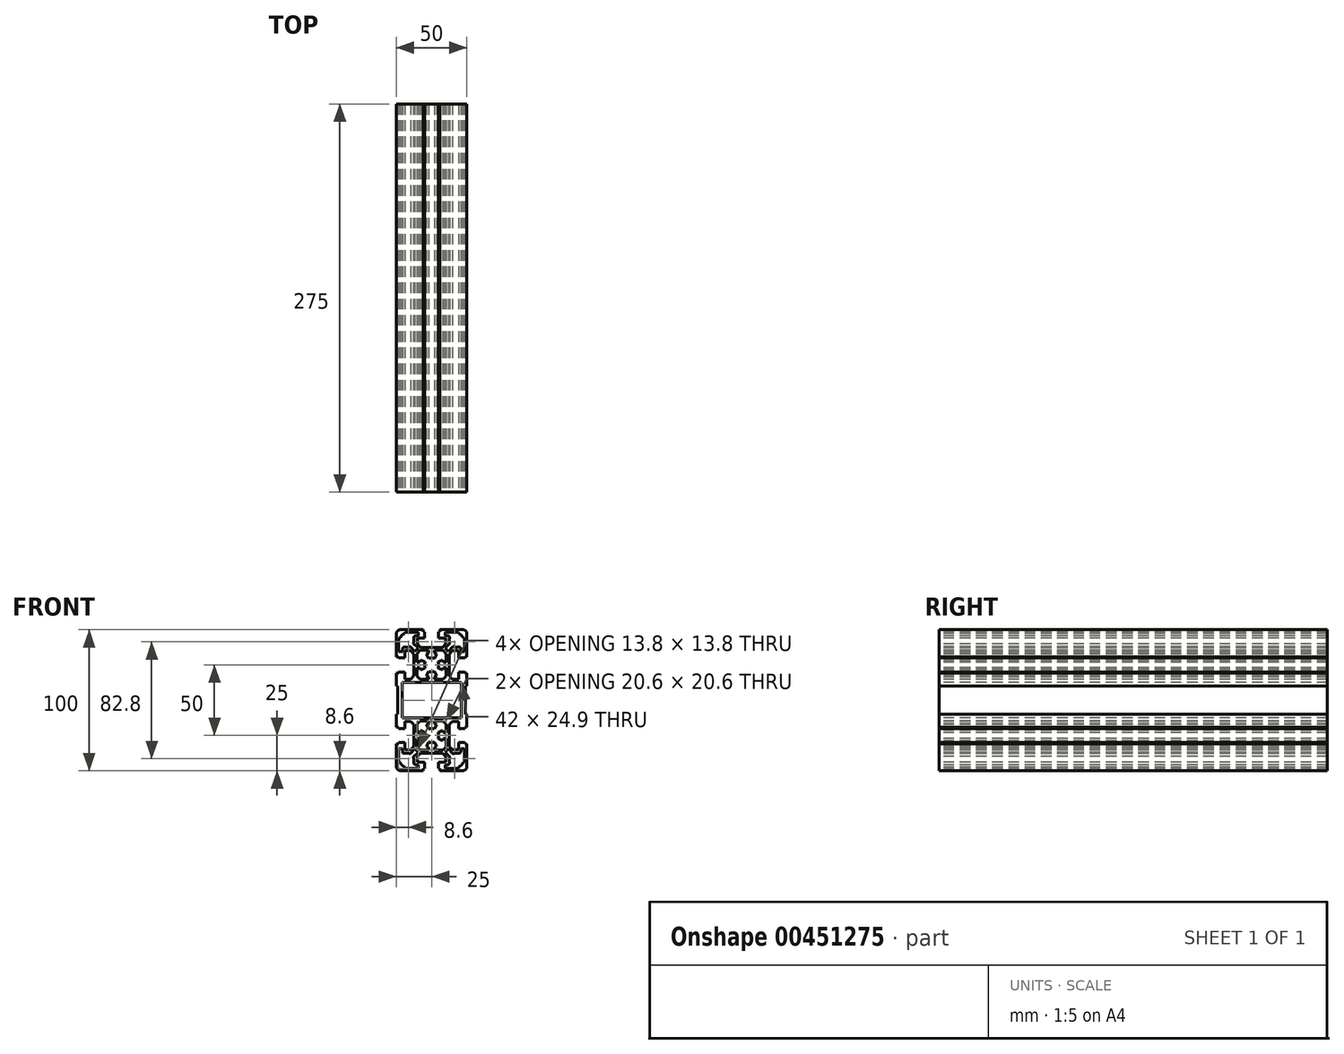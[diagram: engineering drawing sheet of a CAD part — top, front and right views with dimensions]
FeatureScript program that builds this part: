
annotation { "Feature Type Name" : "Feature", "Feature Type Description" : "" }
export const myFeature = defineFeature(function(context is Context, id is Id, definition is map)
    precondition{}
    {
        {
            var Q0;
            Q0=qCreatedBy(makeId("Front.planeOp"),FACE);
            var sketch = newSketch(context, id + "F0", { "sketchPlane" : qUnion([Q0])});
            skLineSegment(sketch, "E0", {"start": v(0, 0) * mm, "end": v(0, 25) * mm, "construction": true});
            skLineSegment(sketch, "E1", {"start": v(0, 0) * mm, "end": v(0, -25) * mm, "construction": true});
            skCircle(sketch, "E2", {"center": v(0, 25) * mm, "radius": 10 * mm});
            skCircle(sketch, "E3", {"center": v(0, -25) * mm, "radius": 10 * mm});
            skLineSegment(sketch, "E4.bottom", {"start": v(25, 50) * mm, "end": v(-25, 50) * mm});
            skLineSegment(sketch, "E4.top", {"start": v(25, -50) * mm, "end": v(-25, -50) * mm});
            skLineSegment(sketch, "E4.left", {"start": v(25, 50) * mm, "end": v(25, -50) * mm});
            skLineSegment(sketch, "E4.right", {"start": v(-25, 50) * mm, "end": v(-25, -50) * mm});
            skPoint(sketch, "E4.middle", {"position": v(0, 0) * mm});
            skSolve(sketch);
        }
        {
            var Q0;
            Q0=makeQuery(id+"F0.imprint","IMPRINT",FACE,{"disambiguationData":[TD([[makeQuery(id+"F0.imprint","IMPRINT",EDGE,{"derivedFrom":sQuery(id+"F0.wireOp",EDGE,"E2")}),-1.0]])]});
            cPlane(context, id + "F1", {"entities" : qUnion([Q0]), "cplaneType" : CPlaneType.OFFSET, "offset" : 25 * mm, "width" : 150 * mm, "height" : 150 * mm});
        }
        {
            var Q0;
            Q0=qCreatedBy(makeId("Front.planeOp"),FACE);
            var sketch = newSketch(context, id + "F2", { "sketchPlane" : qUnion([Q0])});
            skArc(sketch, "E5", {"start": v(-18.8, 37.67) * mm, "mid": v(-20.11, 37.42) * mm, "end": v(-20.7, 36.23) * mm});
            skArc(sketch, "E6", {"start": v(20.7, 36.23) * mm, "mid": v(20.11, 37.42) * mm, "end": v(18.8, 37.67) * mm});
            skArc(sketch, "E7", {"start": v(12.9, -40.52) * mm, "mid": v(12.51, -42.15) * mm, "end": v(12.67, -43.8) * mm});
            skArc(sketch, "E8", {"start": v(22, -50) * mm, "mid": v(24.12, -49.12) * mm, "end": v(25, -47) * mm});
            skArc(sketch, "E9", {"start": v(19, -47.27) * mm, "mid": v(21.04, -46.04) * mm, "end": v(22.27, -44) * mm});
            skArc(sketch, "E10", {"start": v(11.23, -45.7) * mm, "mid": v(12.42, -45.11) * mm, "end": v(12.67, -43.8) * mm});
            skArc(sketch, "E11", {"start": v(18.8, -37.67) * mm, "mid": v(20.11, -37.42) * mm, "end": v(20.7, -36.23) * mm});
            skArc(sketch, "E12", {"start": v(18.8, -37.67) * mm, "mid": v(17.14, -37.51) * mm, "end": v(15.52, -37.9) * mm});
            skArc(sketch, "E13", {"start": v(15.2, -37.85) * mm, "mid": v(15.35, -37.93) * mm, "end": v(15.52, -37.9) * mm});
            skArc(sketch, "E14", {"start": v(12.9, -40.52) * mm, "mid": v(12.93, -40.35) * mm, "end": v(12.84, -40.2) * mm});
            skArc(sketch, "E15", {"start": v(-4.53, -22.89) * mm, "mid": v(-5, -25) * mm, "end": v(-4.53, -27.11) * mm});
            skArc(sketch, "E16", {"start": v(4.53, -27.11) * mm, "mid": v(5, -25) * mm, "end": v(4.53, -22.89) * mm});
            skArc(sketch, "E17", {"start": v(-2.11, -29.53) * mm, "mid": v(0, -30) * mm, "end": v(2.11, -29.53) * mm});
            skArc(sketch, "E18", {"start": v(2.11, -20.47) * mm, "mid": v(0, -20) * mm, "end": v(-2.11, -20.47) * mm});
            skArc(sketch, "E19", {"start": v(-4.53, 27.11) * mm, "mid": v(-5, 25) * mm, "end": v(-4.53, 22.89) * mm});
            skArc(sketch, "E20", {"start": v(4.53, 22.89) * mm, "mid": v(5, 25) * mm, "end": v(4.53, 27.11) * mm});
            skArc(sketch, "E21", {"start": v(-2.11, 20.47) * mm, "mid": v(0, 20) * mm, "end": v(2.11, 20.47) * mm});
            skArc(sketch, "E22", {"start": v(15.52, 37.9) * mm, "mid": v(15.35, 37.93) * mm, "end": v(15.2, 37.84) * mm});
            skArc(sketch, "E23", {"start": v(15.52, 37.9) * mm, "mid": v(17.14, 37.51) * mm, "end": v(18.8, 37.67) * mm});
            skArc(sketch, "E24", {"start": v(2.11, 29.53) * mm, "mid": v(0, 30) * mm, "end": v(-2.11, 29.53) * mm});
            skArc(sketch, "E25", {"start": v(-12.67, -43.8) * mm, "mid": v(-12.51, -42.15) * mm, "end": v(-12.9, -40.52) * mm});
            skArc(sketch, "E26", {"start": v(-25, -47) * mm, "mid": v(-24.12, -49.12) * mm, "end": v(-22, -50) * mm});
            skArc(sketch, "E27", {"start": v(-12.67, -43.8) * mm, "mid": v(-12.42, -45.11) * mm, "end": v(-11.23, -45.7) * mm});
            skArc(sketch, "E28", {"start": v(-22.27, -44) * mm, "mid": v(-21.04, -46.04) * mm, "end": v(-19, -47.27) * mm});
            skArc(sketch, "E29", {"start": v(-20.7, -36.23) * mm, "mid": v(-20.11, -37.42) * mm, "end": v(-18.8, -37.67) * mm});
            skArc(sketch, "E30", {"start": v(-15.52, -37.9) * mm, "mid": v(-17.14, -37.51) * mm, "end": v(-18.8, -37.67) * mm});
            skArc(sketch, "E31", {"start": v(-12.84, -40.2) * mm, "mid": v(-12.93, -40.35) * mm, "end": v(-12.9, -40.52) * mm});
            skArc(sketch, "E32", {"start": v(-15.52, -37.9) * mm, "mid": v(-15.35, -37.93) * mm, "end": v(-15.2, -37.85) * mm});
            skArc(sketch, "E33", {"start": v(-18.8, 37.67) * mm, "mid": v(-17.14, 37.51) * mm, "end": v(-15.52, 37.9) * mm});
            skArc(sketch, "E34", {"start": v(-15.2, 37.84) * mm, "mid": v(-15.35, 37.93) * mm, "end": v(-15.52, 37.9) * mm});
            skArc(sketch, "E35", {"start": v(25, 47) * mm, "mid": v(24.12, 49.12) * mm, "end": v(22, 50) * mm});
            skArc(sketch, "E36", {"start": v(22.27, 44) * mm, "mid": v(21.04, 46.04) * mm, "end": v(19, 47.27) * mm});
            skArc(sketch, "E37", {"start": v(12.67, 43.8) * mm, "mid": v(12.42, 45.11) * mm, "end": v(11.23, 45.7) * mm});
            skArc(sketch, "E38", {"start": v(12.67, 43.8) * mm, "mid": v(12.51, 42.14) * mm, "end": v(12.9, 40.52) * mm});
            skArc(sketch, "E39", {"start": v(12.84, 40.2) * mm, "mid": v(12.93, 40.35) * mm, "end": v(12.9, 40.52) * mm});
            skArc(sketch, "E40", {"start": v(-22, 50) * mm, "mid": v(-24.12, 49.12) * mm, "end": v(-25, 47) * mm});
            skArc(sketch, "E41", {"start": v(-11.23, 45.7) * mm, "mid": v(-12.42, 45.11) * mm, "end": v(-12.67, 43.8) * mm});
            skArc(sketch, "E42", {"start": v(-12.9, 40.52) * mm, "mid": v(-12.93, 40.35) * mm, "end": v(-12.84, 40.2) * mm});
            skArc(sketch, "E43", {"start": v(-12.9, 40.52) * mm, "mid": v(-12.51, 42.14) * mm, "end": v(-12.67, 43.8) * mm});
            skArc(sketch, "E44", {"start": v(-19, 47.27) * mm, "mid": v(-21.04, 46.04) * mm, "end": v(-22.27, 44) * mm});
            skLineSegment(sketch, "E45", {"start": v(-9.54, 36.88) * mm, "end": v(-12.84, 40.2) * mm});
            skLineSegment(sketch, "E46", {"start": v(-25, 47) * mm, "end": v(-25, 30.8) * mm});
            skLineSegment(sketch, "E47", {"start": v(-23.3, 44) * mm, "end": v(-23.3, 34.5) * mm});
            skLineSegment(sketch, "E48", {"start": v(10.05, 39.8) * mm, "end": v(7.75, 37.5) * mm});
            skLineSegment(sketch, "E49", {"start": v(12.84, 40.2) * mm, "end": v(9.54, 36.88) * mm});
            skLineSegment(sketch, "E50", {"start": v(25, 30.8) * mm, "end": v(25, 47) * mm});
            skLineSegment(sketch, "E51", {"start": v(23.3, 34.5) * mm, "end": v(23.3, 44) * mm});
            skLineSegment(sketch, "E52", {"start": v(-7.75, 37.5) * mm, "end": v(-10.05, 39.8) * mm});
            skLineSegment(sketch, "E53", {"start": v(-2, 35.3) * mm, "end": v(-8.01, 35.3) * mm});
            skLineSegment(sketch, "E54", {"start": v(7.75, 37.5) * mm, "end": v(-7.75, 37.5) * mm});
            skLineSegment(sketch, "E55", {"start": v(-4.53, 22.89) * mm, "end": v(-7.7, 21.4) * mm});
            skLineSegment(sketch, "E56", {"start": v(-8.01, 14.7) * mm, "end": v(-2, 14.7) * mm});
            skLineSegment(sketch, "E57", {"start": v(-7.7, 28.6) * mm, "end": v(-4.53, 27.11) * mm});
            skLineSegment(sketch, "E58", {"start": v(-8.01, -35.3) * mm, "end": v(-2, -35.3) * mm});
            skLineSegment(sketch, "E59", {"start": v(-2, -14.7) * mm, "end": v(-8.01, -14.7) * mm});
            skLineSegment(sketch, "E60", {"start": v(-7.7, -21.4) * mm, "end": v(-4.53, -22.89) * mm});
            skLineSegment(sketch, "E61", {"start": v(-4.53, -27.11) * mm, "end": v(-7.7, -28.6) * mm});
            skLineSegment(sketch, "E62", {"start": v(-7.75, -37.5) * mm, "end": v(7.75, -37.5) * mm});
            skLineSegment(sketch, "E63", {"start": v(-5, -44) * mm, "end": v(-10.05, -44) * mm});
            skLineSegment(sketch, "E64", {"start": v(-22, -50) * mm, "end": v(-5.8, -50) * mm});
            skLineSegment(sketch, "E65", {"start": v(21, 12.45) * mm, "end": v(-21, 12.45) * mm});
            skLineSegment(sketch, "E66", {"start": v(-21, -12.45) * mm, "end": v(21, -12.45) * mm});
            skLineSegment(sketch, "E67", {"start": v(24, -10) * mm, "end": v(24, 10) * mm});
            skLineSegment(sketch, "E68", {"start": v(21, -12.45) * mm, "end": v(21, 12.45) * mm});
            skLineSegment(sketch, "E69", {"start": v(-3.6, -32.7) * mm, "end": v(-2.11, -29.53) * mm});
            skLineSegment(sketch, "E70", {"start": v(2.11, -29.53) * mm, "end": v(3.6, -32.7) * mm});
            skLineSegment(sketch, "E71", {"start": v(10.3, -33.01) * mm, "end": v(10.3, -27) * mm});
            skLineSegment(sketch, "E72", {"start": v(12.5, -32.75) * mm, "end": v(12.5, -17.25) * mm});
            skLineSegment(sketch, "E73", {"start": v(19, -30) * mm, "end": v(19, -35.05) * mm});
            skLineSegment(sketch, "E74", {"start": v(25, -47) * mm, "end": v(25, -30.8) * mm});
            skLineSegment(sketch, "E75", {"start": v(10.05, -39.8) * mm, "end": v(10.05, -44) * mm});
            skLineSegment(sketch, "E76", {"start": v(23.3, -44) * mm, "end": v(23.3, -34.5) * mm});
            skLineSegment(sketch, "E77", {"start": v(5.8, -50) * mm, "end": v(22, -50) * mm});
            skLineSegment(sketch, "E78", {"start": v(9.5, -48.3) * mm, "end": v(19, -48.3) * mm});
            skLineSegment(sketch, "E79", {"start": v(22.27, -44) * mm, "end": v(23.3, -44) * mm});
            skLineSegment(sketch, "E80", {"start": v(19, -48.3) * mm, "end": v(19, -47.27) * mm});
            skLineSegment(sketch, "E81", {"start": v(-5.8, -50) * mm, "end": v(-5.8, -48.5) * mm});
            skLineSegment(sketch, "E82", {"start": v(5.8, -48.5) * mm, "end": v(5.8, -50) * mm});
            skLineSegment(sketch, "E83", {"start": v(10.05, -44) * mm, "end": v(5, -44) * mm});
            skLineSegment(sketch, "E84", {"start": v(11.23, -45.7) * mm, "end": v(9.5, -45.7) * mm});
            skLineSegment(sketch, "E85", {"start": v(5, -48.5) * mm, "end": v(5.8, -48.5) * mm});
            skLineSegment(sketch, "E86", {"start": v(5, -44) * mm, "end": v(5, -48.5) * mm});
            skLineSegment(sketch, "E87", {"start": v(9.5, -45.7) * mm, "end": v(9.5, -48.3) * mm});
            skLineSegment(sketch, "E88", {"start": v(-5.8, -48.5) * mm, "end": v(-5, -48.5) * mm});
            skLineSegment(sketch, "E89", {"start": v(-5, -48.5) * mm, "end": v(-5, -44) * mm});
            skLineSegment(sketch, "E90", {"start": v(14.8, -35.05) * mm, "end": v(12.5, -32.75) * mm});
            skLineSegment(sketch, "E91", {"start": v(15.2, -37.85) * mm, "end": v(11.88, -34.54) * mm});
            skLineSegment(sketch, "E92", {"start": v(19, -35.05) * mm, "end": v(14.8, -35.05) * mm});
            skLineSegment(sketch, "E93", {"start": v(20.7, -34.5) * mm, "end": v(20.7, -36.23) * mm});
            skLineSegment(sketch, "E94", {"start": v(23.3, -34.5) * mm, "end": v(20.7, -34.5) * mm});
            skLineSegment(sketch, "E95", {"start": v(9.54, -36.89) * mm, "end": v(12.84, -40.2) * mm});
            skLineSegment(sketch, "E96", {"start": v(7.75, -37.5) * mm, "end": v(10.05, -39.8) * mm});
            skLineSegment(sketch, "E97", {"start": v(3.6, -32.7) * mm, "end": v(2, -33.45) * mm});
            skLineSegment(sketch, "E98", {"start": v(2, -35.3) * mm, "end": v(8.01, -35.3) * mm});
            skLineSegment(sketch, "E99", {"start": v(11.88, -34.54) * mm, "end": v(9.54, -36.89) * mm});
            skLineSegment(sketch, "E100", {"start": v(8.01, -35.3) * mm, "end": v(10.3, -33.01) * mm});
            skLineSegment(sketch, "E101", {"start": v(-2, -35.3) * mm, "end": v(-2, -33.45) * mm});
            skLineSegment(sketch, "E102", {"start": v(-2, -33.45) * mm, "end": v(-3.6, -32.7) * mm});
            skLineSegment(sketch, "E103", {"start": v(2, -33.45) * mm, "end": v(2, -35.3) * mm});
            skLineSegment(sketch, "E104", {"start": v(-2.11, -20.47) * mm, "end": v(-3.6, -17.3) * mm});
            skLineSegment(sketch, "E105", {"start": v(10.3, -23) * mm, "end": v(10.3, -16.99) * mm});
            skLineSegment(sketch, "E106", {"start": v(3.6, -17.3) * mm, "end": v(2.11, -20.47) * mm});
            skLineSegment(sketch, "E107", {"start": v(19, -14.95) * mm, "end": v(19, -20) * mm});
            skLineSegment(sketch, "E108", {"start": v(23.5, -20) * mm, "end": v(23.5, -19.2) * mm});
            skLineSegment(sketch, "E109", {"start": v(25, -30.8) * mm, "end": v(23.5, -30.8) * mm});
            skLineSegment(sketch, "E110", {"start": v(23.5, -30.8) * mm, "end": v(23.5, -30) * mm});
            skLineSegment(sketch, "E111", {"start": v(23.5, -30) * mm, "end": v(19, -30) * mm});
            skLineSegment(sketch, "E112", {"start": v(19, -20) * mm, "end": v(23.5, -20) * mm});
            skLineSegment(sketch, "E113", {"start": v(10.3, -27) * mm, "end": v(8.45, -27) * mm});
            skLineSegment(sketch, "E114", {"start": v(8.45, -27) * mm, "end": v(7.7, -28.6) * mm});
            skLineSegment(sketch, "E115", {"start": v(7.7, -28.6) * mm, "end": v(4.53, -27.11) * mm});
            skLineSegment(sketch, "E116", {"start": v(4.53, -22.89) * mm, "end": v(7.7, -21.4) * mm});
            skLineSegment(sketch, "E117", {"start": v(7.7, -21.4) * mm, "end": v(8.45, -23) * mm});
            skLineSegment(sketch, "E118", {"start": v(8.45, -23) * mm, "end": v(10.3, -23) * mm});
            skLineSegment(sketch, "E119", {"start": v(12.5, -17.25) * mm, "end": v(14.8, -14.95) * mm});
            skLineSegment(sketch, "E120", {"start": v(25, -19.2) * mm, "end": v(25, -10) * mm});
            skLineSegment(sketch, "E121", {"start": v(23.5, -19.2) * mm, "end": v(25, -19.2) * mm});
            skLineSegment(sketch, "E122", {"start": v(14.8, -14.95) * mm, "end": v(19, -14.95) * mm});
            skLineSegment(sketch, "E123", {"start": v(25, -10) * mm, "end": v(24, -10) * mm});
            skLineSegment(sketch, "E124", {"start": v(8.01, -14.7) * mm, "end": v(2, -14.7) * mm});
            skLineSegment(sketch, "E125", {"start": v(2, -16.55) * mm, "end": v(3.6, -17.3) * mm});
            skLineSegment(sketch, "E126", {"start": v(10.3, -16.99) * mm, "end": v(8.01, -14.7) * mm});
            skLineSegment(sketch, "E127", {"start": v(-3.6, -17.3) * mm, "end": v(-2, -16.55) * mm});
            skLineSegment(sketch, "E128", {"start": v(-2, -16.55) * mm, "end": v(-2, -14.7) * mm});
            skLineSegment(sketch, "E129", {"start": v(2, -14.7) * mm, "end": v(2, -16.55) * mm});
            skLineSegment(sketch, "E130", {"start": v(-2, 14.7) * mm, "end": v(-2, 16.55) * mm});
            skLineSegment(sketch, "E131", {"start": v(2, 16.55) * mm, "end": v(2, 14.7) * mm});
            skLineSegment(sketch, "E132", {"start": v(8.01, 14.7) * mm, "end": v(10.3, 16.99) * mm});
            skLineSegment(sketch, "E133", {"start": v(25, 10) * mm, "end": v(25, 19.2) * mm});
            skLineSegment(sketch, "E134", {"start": v(24, 10) * mm, "end": v(25, 10) * mm});
            skLineSegment(sketch, "E135", {"start": v(2, 14.7) * mm, "end": v(8.01, 14.7) * mm});
            skLineSegment(sketch, "E136", {"start": v(12.5, 17.25) * mm, "end": v(12.5, 32.75) * mm});
            skLineSegment(sketch, "E137", {"start": v(14.8, 14.95) * mm, "end": v(12.5, 17.25) * mm});
            skLineSegment(sketch, "E138", {"start": v(25, 19.2) * mm, "end": v(23.5, 19.2) * mm});
            skLineSegment(sketch, "E139", {"start": v(19, 14.95) * mm, "end": v(14.8, 14.95) * mm});
            skLineSegment(sketch, "E140", {"start": v(19, 20) * mm, "end": v(19, 14.95) * mm});
            skLineSegment(sketch, "E141", {"start": v(23.5, 19.2) * mm, "end": v(23.5, 20) * mm});
            skLineSegment(sketch, "E142", {"start": v(23.5, 20) * mm, "end": v(19, 20) * mm});
            skLineSegment(sketch, "E143", {"start": v(10.3, 16.99) * mm, "end": v(10.3, 23) * mm});
            skLineSegment(sketch, "E144", {"start": v(2.11, 20.47) * mm, "end": v(3.6, 17.3) * mm});
            skLineSegment(sketch, "E145", {"start": v(3.6, 17.3) * mm, "end": v(2, 16.55) * mm});
            skLineSegment(sketch, "E146", {"start": v(-2, 16.55) * mm, "end": v(-3.6, 17.3) * mm});
            skLineSegment(sketch, "E147", {"start": v(-3.6, 17.3) * mm, "end": v(-2.11, 20.47) * mm});
            skLineSegment(sketch, "E148", {"start": v(10.3, 23) * mm, "end": v(8.45, 23) * mm});
            skLineSegment(sketch, "E149", {"start": v(8.45, 23) * mm, "end": v(7.7, 21.4) * mm});
            skLineSegment(sketch, "E150", {"start": v(7.7, 21.4) * mm, "end": v(4.53, 22.89) * mm});
            skLineSegment(sketch, "E151", {"start": v(12.5, 32.75) * mm, "end": v(14.8, 35.05) * mm});
            skLineSegment(sketch, "E152", {"start": v(11.88, 34.54) * mm, "end": v(15.2, 37.84) * mm});
            skLineSegment(sketch, "E153", {"start": v(19, 35.05) * mm, "end": v(19, 30) * mm});
            skLineSegment(sketch, "E154", {"start": v(23.5, 30.8) * mm, "end": v(25, 30.8) * mm});
            skLineSegment(sketch, "E155", {"start": v(23.5, 30) * mm, "end": v(23.5, 30.8) * mm});
            skLineSegment(sketch, "E156", {"start": v(19, 30) * mm, "end": v(23.5, 30) * mm});
            skLineSegment(sketch, "E157", {"start": v(14.8, 35.05) * mm, "end": v(19, 35.05) * mm});
            skLineSegment(sketch, "E158", {"start": v(20.7, 34.5) * mm, "end": v(23.3, 34.5) * mm});
            skLineSegment(sketch, "E159", {"start": v(20.7, 36.23) * mm, "end": v(20.7, 34.5) * mm});
            skLineSegment(sketch, "E160", {"start": v(-2.11, 29.53) * mm, "end": v(-3.6, 32.7) * mm});
            skLineSegment(sketch, "E161", {"start": v(10.3, 27) * mm, "end": v(10.3, 33.01) * mm});
            skLineSegment(sketch, "E162", {"start": v(3.6, 32.7) * mm, "end": v(2.11, 29.53) * mm});
            skLineSegment(sketch, "E163", {"start": v(4.53, 27.11) * mm, "end": v(7.7, 28.6) * mm});
            skLineSegment(sketch, "E164", {"start": v(7.7, 28.6) * mm, "end": v(8.45, 27) * mm});
            skLineSegment(sketch, "E165", {"start": v(8.45, 27) * mm, "end": v(10.3, 27) * mm});
            skLineSegment(sketch, "E166", {"start": v(8.01, 35.3) * mm, "end": v(2, 35.3) * mm});
            skLineSegment(sketch, "E167", {"start": v(2, 33.45) * mm, "end": v(3.6, 32.7) * mm});
            skLineSegment(sketch, "E168", {"start": v(10.3, 33.01) * mm, "end": v(8.01, 35.3) * mm});
            skLineSegment(sketch, "E169", {"start": v(9.54, 36.88) * mm, "end": v(11.88, 34.54) * mm});
            skLineSegment(sketch, "E170", {"start": v(-3.6, 32.7) * mm, "end": v(-2, 33.45) * mm});
            skLineSegment(sketch, "E171", {"start": v(2, 35.3) * mm, "end": v(2, 33.45) * mm});
            skLineSegment(sketch, "E172", {"start": v(-2, 33.45) * mm, "end": v(-2, 35.3) * mm});
            skLineSegment(sketch, "E173", {"start": v(-24, 10) * mm, "end": v(-24, -10) * mm});
            skLineSegment(sketch, "E174", {"start": v(-21, 12.45) * mm, "end": v(-21, -12.45) * mm});
            skLineSegment(sketch, "E175", {"start": v(-19, -35.05) * mm, "end": v(-19, -30) * mm});
            skLineSegment(sketch, "E176", {"start": v(-12.5, -17.25) * mm, "end": v(-12.5, -32.75) * mm});
            skLineSegment(sketch, "E177", {"start": v(-10.3, -27) * mm, "end": v(-10.3, -33.01) * mm});
            skLineSegment(sketch, "E178", {"start": v(-25, -30.8) * mm, "end": v(-25, -47) * mm});
            skLineSegment(sketch, "E179", {"start": v(-23.3, -34.5) * mm, "end": v(-23.3, -44) * mm});
            skLineSegment(sketch, "E180", {"start": v(-10.05, -44) * mm, "end": v(-10.05, -39.8) * mm});
            skLineSegment(sketch, "E181", {"start": v(-19, -48.3) * mm, "end": v(-9.5, -48.3) * mm});
            skLineSegment(sketch, "E182", {"start": v(-9.5, -45.7) * mm, "end": v(-11.23, -45.7) * mm});
            skLineSegment(sketch, "E183", {"start": v(-9.5, -48.3) * mm, "end": v(-9.5, -45.7) * mm});
            skLineSegment(sketch, "E184", {"start": v(-23.3, -44) * mm, "end": v(-22.27, -44) * mm});
            skLineSegment(sketch, "E185", {"start": v(-19, -47.27) * mm, "end": v(-19, -48.3) * mm});
            skLineSegment(sketch, "E186", {"start": v(-12.84, -40.2) * mm, "end": v(-9.54, -36.89) * mm});
            skLineSegment(sketch, "E187", {"start": v(-11.88, -34.54) * mm, "end": v(-15.2, -37.85) * mm});
            skLineSegment(sketch, "E188", {"start": v(-10.05, -39.8) * mm, "end": v(-7.75, -37.5) * mm});
            skLineSegment(sketch, "E189", {"start": v(-14.8, -35.05) * mm, "end": v(-19, -35.05) * mm});
            skLineSegment(sketch, "E190", {"start": v(-12.5, -32.75) * mm, "end": v(-14.8, -35.05) * mm});
            skLineSegment(sketch, "E191", {"start": v(-9.54, -36.89) * mm, "end": v(-11.88, -34.54) * mm});
            skLineSegment(sketch, "E192", {"start": v(-10.3, -33.01) * mm, "end": v(-8.01, -35.3) * mm});
            skLineSegment(sketch, "E193", {"start": v(-20.7, -36.23) * mm, "end": v(-20.7, -34.5) * mm});
            skLineSegment(sketch, "E194", {"start": v(-20.7, -34.5) * mm, "end": v(-23.3, -34.5) * mm});
            skLineSegment(sketch, "E195", {"start": v(-23.5, -19.2) * mm, "end": v(-23.5, -20) * mm});
            skLineSegment(sketch, "E196", {"start": v(-19, -20) * mm, "end": v(-19, -14.95) * mm});
            skLineSegment(sketch, "E197", {"start": v(-10.3, -16.99) * mm, "end": v(-10.3, -23) * mm});
            skLineSegment(sketch, "E198", {"start": v(-7.7, -28.6) * mm, "end": v(-8.45, -27) * mm});
            skLineSegment(sketch, "E199", {"start": v(-8.45, -27) * mm, "end": v(-10.3, -27) * mm});
            skLineSegment(sketch, "E200", {"start": v(-23.5, -30.8) * mm, "end": v(-25, -30.8) * mm});
            skLineSegment(sketch, "E201", {"start": v(-23.5, -30) * mm, "end": v(-23.5, -30.8) * mm});
            skLineSegment(sketch, "E202", {"start": v(-19, -30) * mm, "end": v(-23.5, -30) * mm});
            skLineSegment(sketch, "E203", {"start": v(-8.45, -23) * mm, "end": v(-7.7, -21.4) * mm});
            skLineSegment(sketch, "E204", {"start": v(-10.3, -23) * mm, "end": v(-8.45, -23) * mm});
            skLineSegment(sketch, "E205", {"start": v(-23.5, -20) * mm, "end": v(-19, -20) * mm});
            skLineSegment(sketch, "E206", {"start": v(-25, -10) * mm, "end": v(-25, -19.2) * mm});
            skLineSegment(sketch, "E207", {"start": v(-19, -14.95) * mm, "end": v(-14.8, -14.95) * mm});
            skLineSegment(sketch, "E208", {"start": v(-14.8, -14.95) * mm, "end": v(-12.5, -17.25) * mm});
            skLineSegment(sketch, "E209", {"start": v(-8.01, -14.7) * mm, "end": v(-10.3, -16.99) * mm});
            skLineSegment(sketch, "E210", {"start": v(-25, -19.2) * mm, "end": v(-23.5, -19.2) * mm});
            skLineSegment(sketch, "E211", {"start": v(-24, -10) * mm, "end": v(-25, -10) * mm});
            skLineSegment(sketch, "E212", {"start": v(-25, 19.2) * mm, "end": v(-25, 10) * mm});
            skLineSegment(sketch, "E213", {"start": v(-10.3, 16.99) * mm, "end": v(-8.01, 14.7) * mm});
            skLineSegment(sketch, "E214", {"start": v(-25, 10) * mm, "end": v(-24, 10) * mm});
            skLineSegment(sketch, "E215", {"start": v(-12.5, 32.75) * mm, "end": v(-12.5, 17.25) * mm});
            skLineSegment(sketch, "E216", {"start": v(-10.3, 23) * mm, "end": v(-10.3, 16.99) * mm});
            skLineSegment(sketch, "E217", {"start": v(-14.8, 14.95) * mm, "end": v(-19, 14.95) * mm});
            skLineSegment(sketch, "E218", {"start": v(-12.5, 17.25) * mm, "end": v(-14.8, 14.95) * mm});
            skLineSegment(sketch, "E219", {"start": v(-23.5, 19.2) * mm, "end": v(-25, 19.2) * mm});
            skLineSegment(sketch, "E220", {"start": v(-23.5, 20) * mm, "end": v(-23.5, 19.2) * mm});
            skLineSegment(sketch, "E221", {"start": v(-19, 14.95) * mm, "end": v(-19, 20) * mm});
            skLineSegment(sketch, "E222", {"start": v(-19, 20) * mm, "end": v(-23.5, 20) * mm});
            skLineSegment(sketch, "E223", {"start": v(-7.7, 21.4) * mm, "end": v(-8.45, 23) * mm});
            skLineSegment(sketch, "E224", {"start": v(-8.45, 23) * mm, "end": v(-10.3, 23) * mm});
            skLineSegment(sketch, "E225", {"start": v(-10.3, 33.01) * mm, "end": v(-10.3, 27) * mm});
            skLineSegment(sketch, "E226", {"start": v(-19, 30) * mm, "end": v(-19, 35.05) * mm});
            skLineSegment(sketch, "E227", {"start": v(-8.45, 27) * mm, "end": v(-7.7, 28.6) * mm});
            skLineSegment(sketch, "E228", {"start": v(-10.3, 27) * mm, "end": v(-8.45, 27) * mm});
            skLineSegment(sketch, "E229", {"start": v(-23.5, 30.8) * mm, "end": v(-23.5, 30) * mm});
            skLineSegment(sketch, "E230", {"start": v(-25, 30.8) * mm, "end": v(-23.5, 30.8) * mm});
            skLineSegment(sketch, "E231", {"start": v(-23.5, 30) * mm, "end": v(-19, 30) * mm});
            skLineSegment(sketch, "E232", {"start": v(-19, 35.05) * mm, "end": v(-14.8, 35.05) * mm});
            skLineSegment(sketch, "E233", {"start": v(-14.8, 35.05) * mm, "end": v(-12.5, 32.75) * mm});
            skLineSegment(sketch, "E234", {"start": v(-15.2, 37.84) * mm, "end": v(-11.88, 34.54) * mm});
            skLineSegment(sketch, "E235", {"start": v(-11.88, 34.54) * mm, "end": v(-9.54, 36.88) * mm});
            skLineSegment(sketch, "E236", {"start": v(-8.01, 35.3) * mm, "end": v(-10.3, 33.01) * mm});
            skLineSegment(sketch, "E237", {"start": v(-23.3, 34.5) * mm, "end": v(-20.7, 34.5) * mm});
            skLineSegment(sketch, "E238", {"start": v(-20.7, 34.5) * mm, "end": v(-20.7, 36.23) * mm});
            skLineSegment(sketch, "E239", {"start": v(-5.8, 50) * mm, "end": v(-22, 50) * mm});
            skLineSegment(sketch, "E240", {"start": v(-10.05, 44) * mm, "end": v(-5, 44) * mm});
            skLineSegment(sketch, "E241", {"start": v(-5.8, 48.5) * mm, "end": v(-5.8, 50) * mm});
            skLineSegment(sketch, "E242", {"start": v(5.8, 50) * mm, "end": v(5.8, 48.5) * mm});
            skLineSegment(sketch, "E243", {"start": v(19, 48.3) * mm, "end": v(9.5, 48.3) * mm});
            skLineSegment(sketch, "E244", {"start": v(19, 47.27) * mm, "end": v(19, 48.3) * mm});
            skLineSegment(sketch, "E245", {"start": v(23.3, 44) * mm, "end": v(22.27, 44) * mm});
            skLineSegment(sketch, "E246", {"start": v(10.05, 44) * mm, "end": v(10.05, 39.8) * mm});
            skLineSegment(sketch, "E247", {"start": v(5, 44) * mm, "end": v(10.05, 44) * mm});
            skLineSegment(sketch, "E248", {"start": v(5, 48.5) * mm, "end": v(5, 44) * mm});
            skLineSegment(sketch, "E249", {"start": v(5.8, 48.5) * mm, "end": v(5, 48.5) * mm});
            skLineSegment(sketch, "E250", {"start": v(9.5, 48.3) * mm, "end": v(9.5, 45.7) * mm});
            skLineSegment(sketch, "E251", {"start": v(9.5, 45.7) * mm, "end": v(11.23, 45.7) * mm});
            skLineSegment(sketch, "E252", {"start": v(-5, 48.5) * mm, "end": v(-5.8, 48.5) * mm});
            skLineSegment(sketch, "E253", {"start": v(-5, 44) * mm, "end": v(-5, 48.5) * mm});
            skLineSegment(sketch, "E254", {"start": v(22, 50) * mm, "end": v(5.8, 50) * mm});
            skLineSegment(sketch, "E255", {"start": v(-10.05, 39.8) * mm, "end": v(-10.05, 44) * mm});
            skLineSegment(sketch, "E256", {"start": v(-9.5, 48.3) * mm, "end": v(-19, 48.3) * mm});
            skLineSegment(sketch, "E257", {"start": v(-11.23, 45.7) * mm, "end": v(-9.5, 45.7) * mm});
            skLineSegment(sketch, "E258", {"start": v(-9.5, 45.7) * mm, "end": v(-9.5, 48.3) * mm});
            skLineSegment(sketch, "E259", {"start": v(-22.27, 44) * mm, "end": v(-23.3, 44) * mm});
            skLineSegment(sketch, "E260", {"start": v(-19, 48.3) * mm, "end": v(-19, 47.27) * mm});
            skLineSegment(sketch, "E261", {"start": v(31.28, 0) * mm, "end": v(-51.84, 0) * mm});
            skLineSegment(sketch, "E262", {"start": v(0, 67.76) * mm, "end": v(0, -64.44) * mm});
            skSolve(sketch);
        }
        {
            var Q0;
            Q0=makeQuery(id+"F2.imprint","IMPRINT",FACE,{"disambiguationData":[TD([[makeQuery(id+"F2.imprint","IMPRINT",EDGE,{"derivedFrom":sQuery(id+"F2.wireOp",EDGE,"E6")}),1.0]])]});
            var Q1;
            Q1=makeQuery(id+"F2.imprint","IMPRINT",FACE,{"disambiguationData":[TD([[makeQuery(id+"F2.imprint","IMPRINT",EDGE,{"derivedFrom":sQuery(id+"F2.wireOp",EDGE,"E5")}),1.0]])]});
            var Q2;
            Q2=makeQuery(id+"F2.imprint","IMPRINT",FACE,{"disambiguationData":[TD([[makeQuery(id+"F2.imprint","IMPRINT",EDGE,{"derivedFrom":sQuery(id+"F2.wireOp",EDGE,"E7")}),-1.0]])]});
            var Q3;
            Q3=makeQuery(id+"F2.imprint","IMPRINT",FACE,{"disambiguationData":[TD([[makeQuery(id+"F2.imprint","IMPRINT",EDGE,{"derivedFrom":sQuery(id+"F2.wireOp",EDGE,"E15")}),-1.0]])]});
            extrude(context, id + "F3", {"entities" : qUnion([Q0, Q1, Q2, Q3]), "oppositeDirection" : true, "depth" : 275 * mm});
        }
    });
